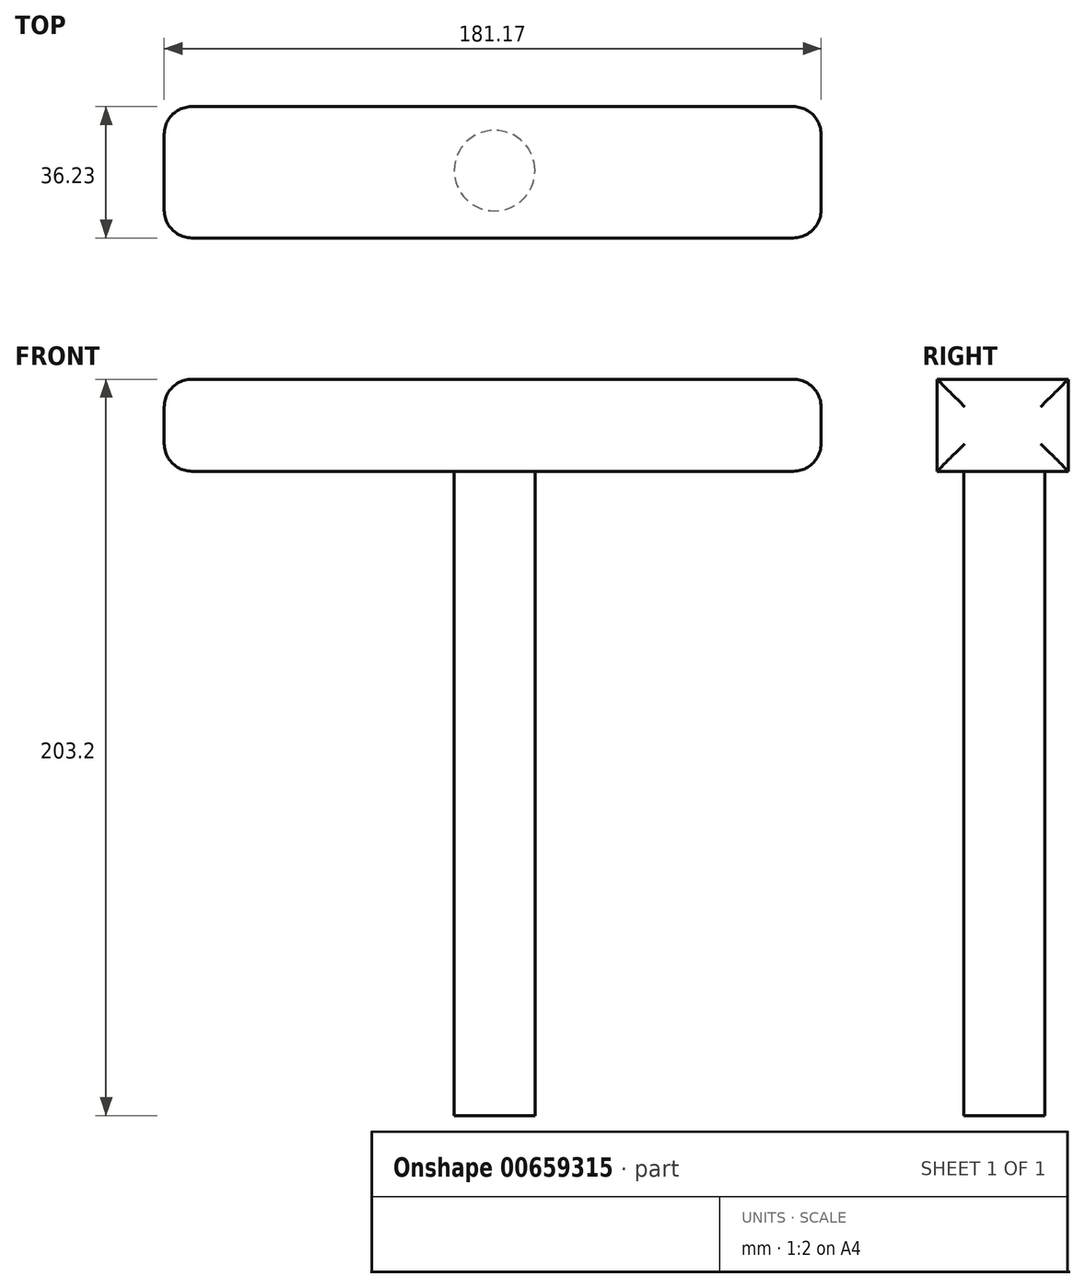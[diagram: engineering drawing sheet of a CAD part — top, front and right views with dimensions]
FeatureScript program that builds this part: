
annotation { "Feature Type Name" : "Feature", "Feature Type Description" : "" }
export const myFeature = defineFeature(function(context is Context, id is Id, definition is map)
    precondition{}
    {
        {
            var Q0;
            Q0=qCreatedBy(makeId("Top.planeOp"),FACE);
            var sketch = newSketch(context, id + "F0", { "sketchPlane" : qUnion([Q0])});
            skLineSegment(sketch, "E0.bottom", {"start": v(-40.34, -18.56) * mm, "end": v(39.23, -18.56) * mm});
            skLineSegment(sketch, "E0.top", {"start": v(-40.34, 17.67) * mm, "end": v(39.23, 17.67) * mm});
            skLineSegment(sketch, "E0.left", {"start": v(-40.34, -18.56) * mm, "end": v(-40.34, 17.67) * mm});
            skLineSegment(sketch, "E0.right", {"start": v(39.23, -18.56) * mm, "end": v(39.23, 17.67) * mm});
            skSolve(sketch);
        }
        {
            var Q0;
            Q0=makeQuery(id+"F0.imprint","IMPRINT",FACE,{"disambiguationData":[TD([[makeQuery(id+"F0.imprint","IMPRINT",EDGE,{"derivedFrom":sQuery(id+"F0.wireOp",EDGE,"E0.bottom")}),1.0]])]});
            extrude(context, id + "F1", {"entities" : qUnion([Q0]), "depth" : 12.7 * mm, "offsetDistance" : 25.4 * mm});
        }
        {
            var Q0;
            Q0=makeQuery(id+"F1.opExtrude","CAP_FACE",FACE,{"disambiguationData":[OSD([sQuery(id+"F0.wireOp",EDGE,"E0.bottom"),sQuery(id+"F0.wireOp",EDGE,"E0.top"),sQuery(id+"F0.wireOp",EDGE,"E0.left"),sQuery(id+"F0.wireOp",EDGE,"E0.right")])],"isStart":true});
            extrude(context, id + "F2", {"entities" : qUnion([Q0]), "operationType" : NewBodyOperationType.ADD, "depth" : 12.7 * mm, "offsetDistance" : 25.4 * mm});
        }
        {
            var Q0;
            Q0=makeQuery(id+"F2.opExtrude","CAP_FACE",FACE,{"disambiguationData":[OSD([sQuery(id+"F0.wireOp",EDGE,"E0.bottom"),sQuery(id+"F0.wireOp",EDGE,"E0.top"),sQuery(id+"F0.wireOp",EDGE,"E0.left"),sQuery(id+"F0.wireOp",EDGE,"E0.right")])],"isStart":false});
            var sketch = newSketch(context, id + "F3", { "sketchPlane" : qUnion([Q0])});
            skCircle(sketch, "E1", {"center": v(0, 0) * mm, "radius": 11.13 * mm});
            skSolve(sketch);
        }
        {
            var Q0;
            Q0=makeQuery(id+"F3.imprint","IMPRINT",FACE,{"disambiguationData":[TD([[makeQuery(id+"F3.imprint","IMPRINT",EDGE,{"derivedFrom":sQuery(id+"F3.wireOp",EDGE,"E1")}),1.0]])]});
            extrude(context, id + "F4", {"entities" : qUnion([Q0]), "operationType" : NewBodyOperationType.ADD, "depth" : 177.8 * mm, "offsetDistance" : 25.4 * mm});
        }
        {
            var Q0;
            {var subQ0=sQuery(id+"F0.wireOp",EDGE,"E0.left");Q0=makeQuery(id+"F2.boolean.opBoolean","MERGE",FACE,{"derivedFrom":[makeQuery(id+"F1.opExtrude","SWEPT_FACE",FACE,{"disambiguationData":[OSD([subQ0])]}),makeQuery(id+"F2.opExtrude","SWEPT_FACE",FACE,{"disambiguationData":[OSD([subQ0])]})]});}
            extrude(context, id + "F5", {"entities" : qUnion([Q0]), "operationType" : NewBodyOperationType.ADD, "depth" : 50.8 * mm, "offsetDistance" : 25.4 * mm});
        }
        {
            var Q0;
            {var subQ0=sQuery(id+"F0.wireOp",EDGE,"E0.right");Q0=makeQuery(id+"F2.boolean.opBoolean","MERGE",FACE,{"derivedFrom":[makeQuery(id+"F1.opExtrude","SWEPT_FACE",FACE,{"disambiguationData":[OSD([subQ0])]}),makeQuery(id+"F2.opExtrude","SWEPT_FACE",FACE,{"disambiguationData":[OSD([subQ0])]})]});}
            extrude(context, id + "F6", {"entities" : qUnion([Q0]), "operationType" : NewBodyOperationType.ADD, "depth" : 50.8 * mm, "offsetDistance" : 25.4 * mm});
        }
        {
            var Q0;
            Q0=makeQuery(id+"F6.opExtrude","CAP_FACE",FACE,{"disambiguationData":[OSD([sQuery(id+"F0.wireOp",EDGE,"E0.right")])],"isStart":false});
            fillet(context, id + "F7", {"entities" : qUnion([Q0]), "radius" : 7.62 * mm, "tangentPropagation" : true, "allowEdgeOverflow" : false});
        }
        {
            var Q0;
            Q0=makeQuery(id+"F5.opExtrude","CAP_FACE",FACE,{"disambiguationData":[OSD([sQuery(id+"F0.wireOp",EDGE,"E0.left")])],"isStart":false});
            fillet(context, id + "F8", {"entities" : qUnion([Q0]), "radius" : 7.62 * mm, "tangentPropagation" : true, "allowEdgeOverflow" : false});
        }
    });
